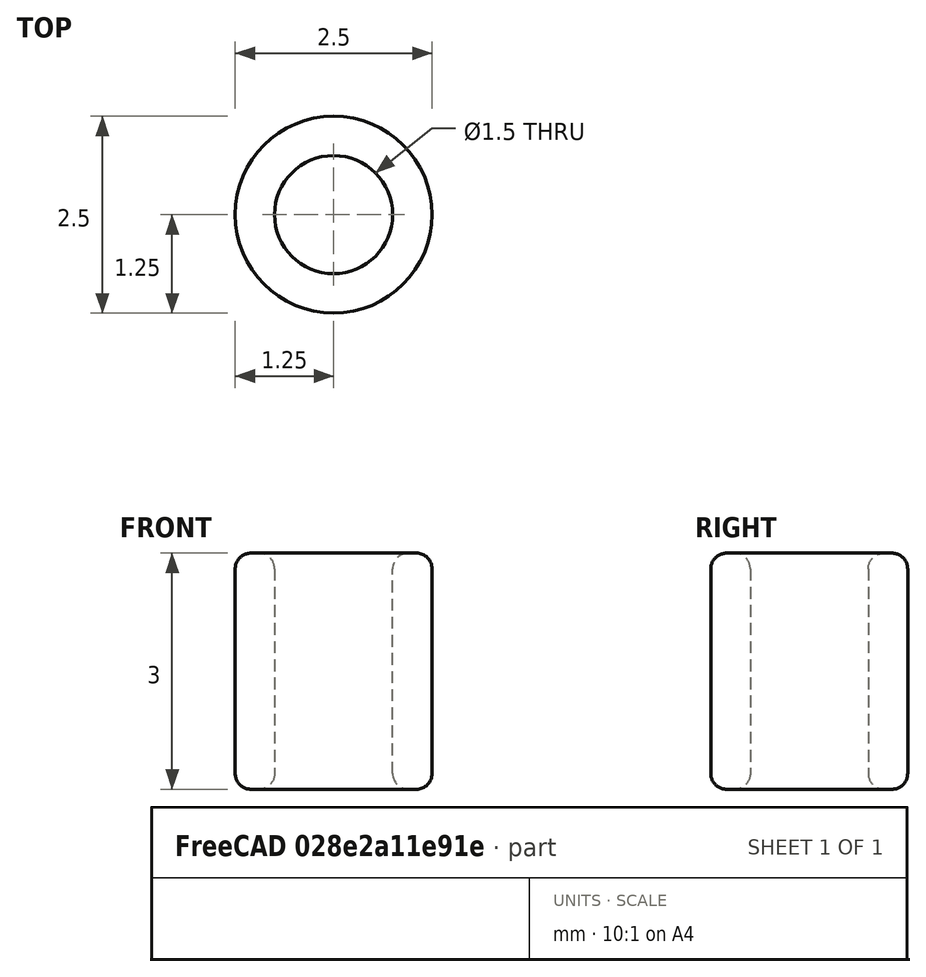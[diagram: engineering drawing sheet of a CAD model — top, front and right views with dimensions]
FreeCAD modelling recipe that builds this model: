
FCSTD DOCUMENT  (FreeCAD 1.0R39285 (Git))
Label: HairclipEnd
License: All rights reserved
LicenseURL: https://en.wikipedia.org/wiki/All_rights_reserved
objects: Sketcher::SketchObject×1, PartDesign::Pad×1, PartDesign::Fillet×1, PartDesign::Body×1
note: 9 computed .brp shape members not serialized (recipe doc carries the construction recipe); baked Part::Feature solids carry a one-line shape summary decoded from their .brp

FEATURE [Sketcher::SketchObject] Sketch
  ArcFitTolerance = 1e-06
  AttachmentSupport = -> [XY_Plane]
  FullyConstrained = true
  MakeInternals = false
  MapMode = 5
  sketch-geometry (2):
    g0: Circle CenterX=0 CenterY=0 CenterZ=0 NormalX=0 NormalY=0 NormalZ=1 AngleXU=0 Radius=0.75
    g1: Circle CenterX=0 CenterY=0 CenterZ=0 NormalX=0 NormalY=0 NormalZ=1 AngleXU=0 Radius=1.25
  constraints (4):
    c: Coincident(g0,g-1)
    c: Coincident(g1,g0)
    c: Diameter(g0) = 1.5
    c: Diameter(g1) = 2.5
FEATURE [PartDesign::Pad] Pad
  Direction = (0,0,1)
  Length = 3
  Length2 = 10
  Profile = -> Sketch
  ReferenceAxis = -> Sketch [N_Axis]
  Refine = true
  Suppressed = false
  Type = 0
FEATURE [PartDesign::Fillet] Fillet
  Base = -> Pad [Edge1,Edge2,Edge3,Edge4,Edge5,Edge6]
  BaseFeature = -> Pad
  Radius = 0.2
  Refine = true
  SupportTransform = false
  Suppressed = false
  UseAllEdges = true
FEATURE [PartDesign::Body] Body
  AllowCompound = false
  Group = -> [Sketch,Pad,Fillet]
  Origin = -> Origin
  Tip = -> Fillet
